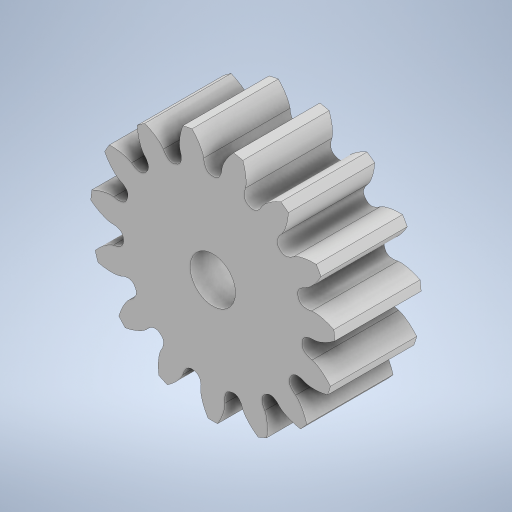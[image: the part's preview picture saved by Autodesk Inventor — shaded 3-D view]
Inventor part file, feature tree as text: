
AUTODESK INVENTOR PART (.ipt)
format: ipt  version: 2023 (Build 270158000, 158)  size: 395,776 bytes
history: native  units: mm
features: sketch x2, extrude x2, pattern_circular x1, hole x1
ambient origin geometry x8: Origin, YZ Plane, XZ Plane, XY Plane, X Axis, Y Axis, Z Axis, Center Point
bodies: Solid1 (feature_tree)
feature tree (6):
  sketch  "Sketch1"  dims[d0=12.0mm d1=0.0mm]
  extrude  "Extrusion1"  TaperAngle=0.0deg  [1 undecoded]
  extrude  "Extrusion2"  Depth=150.0mm TaperAngle=360.0deg
  pattern_circular  "Circular Pattern2"  [2 undecoded]
  hole  "Hole1"  [1 undecoded]
  sketch  "Sketch2"  dims[d2=0.0mm d3=0.0mm d7=150.0mm d8=360.0deg d10=6.32mm d11=6.0mm d12=8.0mm d13=2.0mm d14=90.0deg d15=8.0mm d16=20.594885mm]
note: 4 required parameter values undecoded (feature->parameter linkage not recoverable at this tier; creation-order binding heuristic only, values carry confidence <= 0.55)
